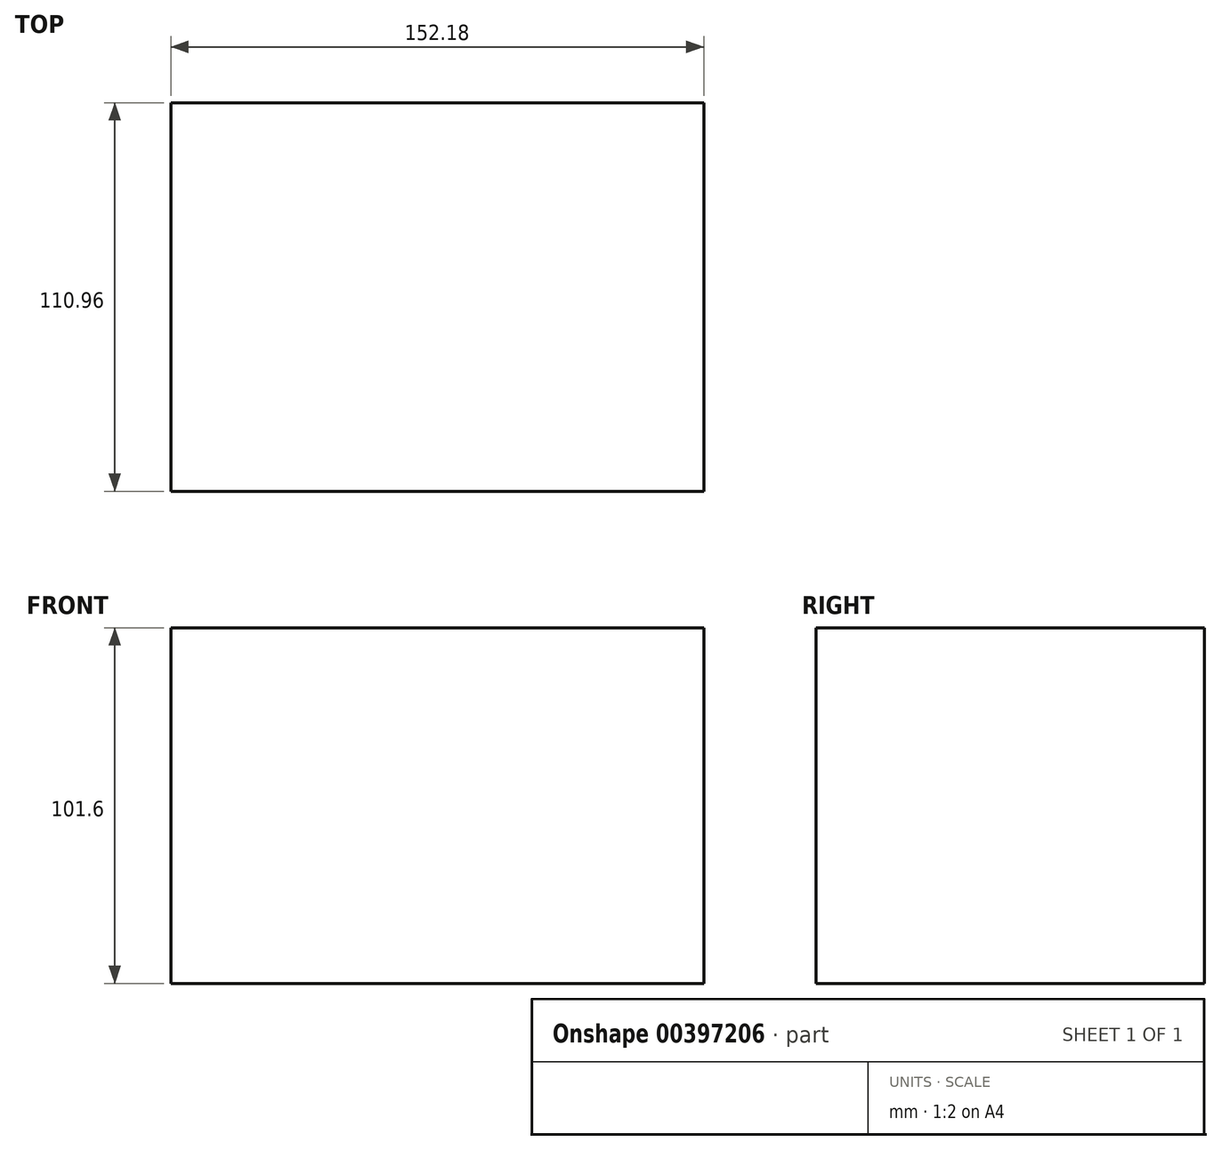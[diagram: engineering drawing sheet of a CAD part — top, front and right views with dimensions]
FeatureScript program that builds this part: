
annotation { "Feature Type Name" : "Feature", "Feature Type Description" : "" }
export const myFeature = defineFeature(function(context is Context, id is Id, definition is map)
    precondition{}
    {
        {
            var Q0;
            Q0=qCreatedBy(makeId("Top.planeOp"),FACE);
            var sketch = newSketch(context, id + "F0", { "sketchPlane" : qUnion([Q0])});
            skLineSegment(sketch, "E0.bottom", {"start": v(-76.09, 55.6) * mm, "end": v(76.09, 55.6) * mm});
            skLineSegment(sketch, "E0.top", {"start": v(-76.09, -55.37) * mm, "end": v(76.09, -55.37) * mm});
            skLineSegment(sketch, "E0.left", {"start": v(-76.09, 55.6) * mm, "end": v(-76.09, -55.37) * mm});
            skLineSegment(sketch, "E0.right", {"start": v(76.09, 55.6) * mm, "end": v(76.09, -55.37) * mm});
            skSolve(sketch);
        }
        {
            var Q0;
            Q0 = qSketchRegion(id + "F0", true);
            extrude(context, id + "F1", {"entities" : qUnion([Q0]), "depth" : 101.6 * mm});
        }
    });
